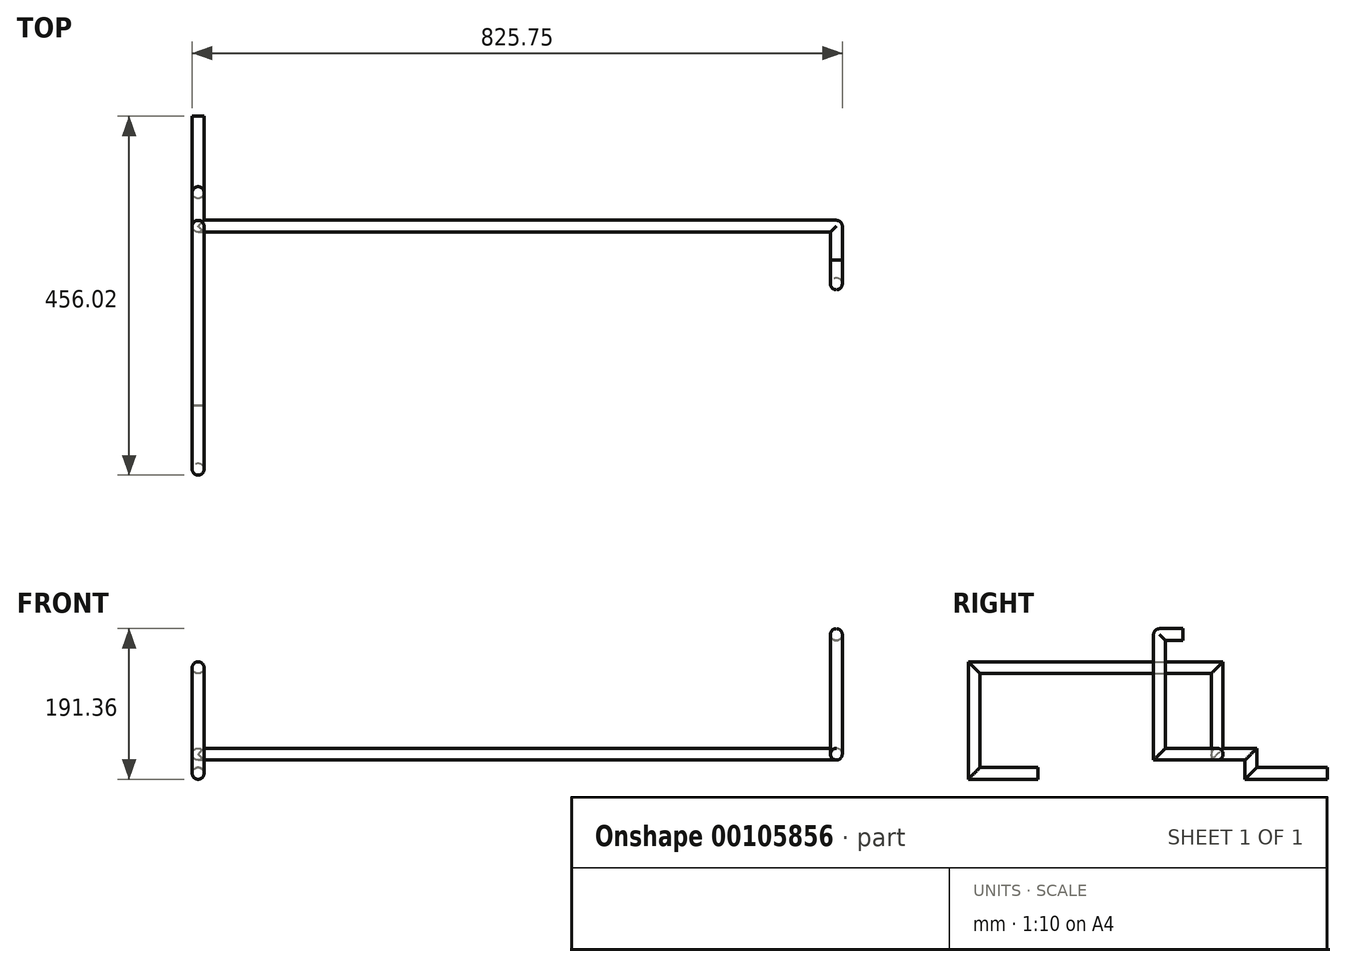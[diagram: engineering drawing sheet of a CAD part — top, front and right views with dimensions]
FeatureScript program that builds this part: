
annotation { "Feature Type Name" : "Feature", "Feature Type Description" : "" }
export const myFeature = defineFeature(function(context is Context, id is Id, definition is map)
    precondition{}
    {
        {
            var Q0;
            Q0=qCreatedBy(makeId("Front.planeOp"),FACE);
            var sketch = newSketch(context, id + "F0", { "sketchPlane" : qUnion([Q0])});
            skCircle(sketch, "E0", {"center": v(0, 0) * mm, "radius": 7.5 * mm});
            skSolve(sketch);
        }
        {
            var Q0;
            Q0=qCreatedBy(makeId("Right.planeOp"),FACE);
            var sketch = newSketch(context, id + "F1", { "sketchPlane" : qUnion([Q0])});
            skLineSegment(sketch, "E1", {"start": v(-80.78, 0) * mm, "end": v(0, 0) * mm});
            skLineSegment(sketch, "E2", {"start": v(-80.78, 0) * mm, "end": v(-80.78, 134.38) * mm});
            skLineSegment(sketch, "E3", {"start": v(-80.78, 134.38) * mm, "end": v(228, 134.38) * mm});
            skLineSegment(sketch, "E4", {"start": v(228, 134.38) * mm, "end": v(228, 24.38) * mm});
            skLineSegment(sketch, "E5", {"start": v(228, 24.38) * mm, "end": v(270.74, 24.38) * mm});
            skLineSegment(sketch, "E6", {"start": v(270.74, 24.38) * mm, "end": v(270.74, 0) * mm});
            skLineSegment(sketch, "E7", {"start": v(270.74, 0) * mm, "end": v(367.74, 0) * mm});
            skSolve(sketch);
        }
        {
            var Q0;
            Q0=makeQuery(id+"F0.imprint","IMPRINT",FACE,{"disambiguationData":[TD([[makeQuery(id+"F0.imprint","IMPRINT",EDGE,{"derivedFrom":sQuery(id+"F0.wireOp",EDGE,"E0")}),1.0]])]});
            var Q1;
            Q1=sQuery(id+"F1.wireOp",EDGE,"E1");
            var Q2;
            Q2=sQuery(id+"F1.wireOp",EDGE,"E2");
            var Q3;
            Q3=sQuery(id+"F1.wireOp",EDGE,"E3");
            var Q4;
            Q4=sQuery(id+"F1.wireOp",EDGE,"E4");
            var Q5;
            Q5=sQuery(id+"F1.wireOp",EDGE,"E5");
            var Q6;
            Q6=sQuery(id+"F1.wireOp",EDGE,"E6");
            var Q7;
            Q7=sQuery(id+"F1.wireOp",EDGE,"E7");
            sweep(context, id + "F2", {"profiles" : qUnion([Q0]), "path" : qUnion([Q1, Q2, Q3, Q4, Q5, Q6, Q7])});
        }
        {
            var Q0;
            Q0=qCreatedBy(makeId("Right.planeOp"),FACE);
            var sketch = newSketch(context, id + "F3", { "sketchPlane" : qUnion([Q0])});
            skCircle(sketch, "E8", {"center": v(228, 24.38) * mm, "radius": 7.5 * mm});
            skSolve(sketch);
        }
        {
            var Q0;
            Q0=qCreatedBy(makeId("Front.planeOp"),FACE);
            var sketch = newSketch(context, id + "F4", { "sketchPlane" : qUnion([Q0])});
            skLineSegment(sketch, "E9", {"start": v(0, 0) * mm, "end": v(810.75, 0) * mm});
            skSolve(sketch);
        }
        {
            var Q0;
            Q0=qSketchRegion(id+"F3",true);
            var Q1;
            Q1=sQuery(id+"F4.wireOp",EDGE,"E9");
            sweep(context, id + "F5", {"operationType" : NewBodyOperationType.ADD, "profiles" : qUnion([Q0]), "path" : qUnion([Q1])});
        }
        {
            var Q0;
            Q0=qCreatedBy(makeId("Front.planeOp"),FACE);
            cPlane(context, id + "F6", {"entities" : qUnion([Q0]), "cplaneType" : CPlaneType.OFFSET, "offset" : 228 * mm, "oppositeDirection" : true, "width" : 150 * mm, "height" : 150 * mm});
        }
        {
            var Q0;
            Q0=qCreatedBy(id+"F6.planeOp",FACE);
            var sketch = newSketch(context, id + "F7", { "sketchPlane" : qUnion([Q0])});
            skCircle(sketch, "E10", {"center": v(810.75, 24.38) * mm, "radius": 7.5 * mm});
            skSolve(sketch);
        }
        {
            var Q0;
            Q0=qCreatedBy(makeId("Right.planeOp"),FACE);
            var sketch = newSketch(context, id + "F8", { "sketchPlane" : qUnion([Q0])});
            skLineSegment(sketch, "E11", {"start": v(228, 24.38) * mm, "end": v(154.71, 24.38) * mm});
            skLineSegment(sketch, "E12", {"start": v(154.71, 24.38) * mm, "end": v(154.71, 176.36) * mm});
            skSolve(sketch);
        }
        {
            var Q0;
            Q0=makeQuery(id+"F7.imprint","IMPRINT",FACE,{"disambiguationData":[TD([[makeQuery(id+"F7.imprint","IMPRINT",EDGE,{"derivedFrom":sQuery(id+"F7.wireOp",EDGE,"E10")}),1.0]])]});
            var Q1;
            Q1=sQuery(id+"F8.wireOp",EDGE,"E11");
            var Q2;
            Q2=sQuery(id+"F8.wireOp",EDGE,"E12");
            sweep(context, id + "F9", {"operationType" : NewBodyOperationType.ADD, "profiles" : qUnion([Q0]), "path" : qUnion([Q1, Q2])});
        }
        {
            var Q0;
            Q0=qCreatedBy(makeId("Front.planeOp"),FACE);
            cPlane(context, id + "F10", {"entities" : qUnion([Q0]), "cplaneType" : CPlaneType.OFFSET, "offset" : 154.71 * mm, "oppositeDirection" : true, "width" : 150 * mm, "height" : 150 * mm});
        }
        {
            var Q0;
            Q0=qCreatedBy(id+"F10.planeOp",FACE);
            var sketch = newSketch(context, id + "F11", { "sketchPlane" : qUnion([Q0])});
            skCircle(sketch, "E13", {"center": v(810.75, 176.36) * mm, "radius": 7.5 * mm});
            skSolve(sketch);
        }
        {
            var Q0;
            Q0=qCreatedBy(makeId("Top.planeOp"),FACE);
            var sketch = newSketch(context, id + "F12", { "sketchPlane" : qUnion([Q0])});
            skLineSegment(sketch, "E14", {"start": v(862, 154.71) * mm, "end": v(862, 184.71) * mm});
            skSolve(sketch);
        }
        {
            var Q0;
            Q0=makeQuery(id+"F9.opSweep","CAP_FACE",FACE,{"disambiguationData":[OSD([sQuery(id+"F7.wireOp",EDGE,"E10"),sQuery(id+"F8.wireOp",VERTEX,"E11.start")])],"isStart":true});
            var Q1;
            Q1=makeQuery(id+"F9.boolean.opBoolean","INTERSECT",EDGE,{"derivedFrom":[makeQuery(id+"F5.opSweep","CAP_FACE",FACE,{"disambiguationData":[OSD([sQuery(id+"F3.wireOp",EDGE,"E8"),sQuery(id+"F4.wireOp",VERTEX,"E9.end")])],"isStart":false}),makeQuery(id+"F9.opSweep","CAP_FACE",FACE,{"disambiguationData":[OSD([sQuery(id+"F7.wireOp",EDGE,"E10"),sQuery(id+"F8.wireOp",VERTEX,"E11.start")])],"isStart":true})]});
            revolve(context, id + "F13", {"operationType" : NewBodyOperationType.ADD, "entities" : qUnion([Q0]), "axis" : qUnion([Q1]), "revolveType" : RevolveType.FULL});
        }
        {
            var Q0;
            Q0=makeQuery(id+"F11.imprint","IMPRINT",FACE,{"disambiguationData":[TD([[makeQuery(id+"F11.imprint","IMPRINT",EDGE,{"derivedFrom":sQuery(id+"F11.wireOp",EDGE,"E13")}),1.0]])]});
            var Q1;
            Q1=sQuery(id+"F12.wireOp",EDGE,"E14");
            sweep(context, id + "F14", {"operationType" : NewBodyOperationType.ADD, "profiles" : qUnion([Q0]), "path" : qUnion([Q1])});
        }
        {
            var Q0;
            Q0=makeQuery(id+"F9.opSweep","CAP_FACE",FACE,{"disambiguationData":[OSD([sQuery(id+"F7.wireOp",EDGE,"E10"),sQuery(id+"F8.wireOp",VERTEX,"E12.end")])],"isStart":false});
            var Q1;
            Q1=makeQuery(id+"F14.boolean.opBoolean","INTERSECT",EDGE,{"derivedFrom":[makeQuery(id+"F9.opSweep","CAP_FACE",FACE,{"disambiguationData":[OSD([sQuery(id+"F7.wireOp",EDGE,"E10"),sQuery(id+"F8.wireOp",VERTEX,"E12.end")])],"isStart":false}),makeQuery(id+"F14.opSweep","CAP_FACE",FACE,{"disambiguationData":[OSD([sQuery(id+"F11.wireOp",EDGE,"E13"),sQuery(id+"F12.wireOp",VERTEX,"E14.start")])],"isStart":true})]});
            revolve(context, id + "F15", {"operationType" : NewBodyOperationType.ADD, "entities" : qUnion([Q0]), "axis" : qUnion([Q1]), "revolveType" : RevolveType.FULL});
        }
    });
